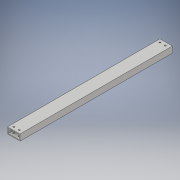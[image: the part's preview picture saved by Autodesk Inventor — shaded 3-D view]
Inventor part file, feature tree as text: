
AUTODESK INVENTOR PART (.ipt)
format: ipt  version: 2017 (Build 210142000, 142)  size: 122,880 bytes
history: native  units: in
note: dims shown in document units (in); Inventor stores cm internally (conversion verified against a paired STEP export)
features: sketch x2, extrude x1, hole x1
ambient origin geometry x8: Origin, YZ Plane, XZ Plane, XY Plane, X Axis, Y Axis, Z Axis, Center Point
bodies: Solid1 (feature_tree)
feature tree (4):
  extrude  "Extrusion1"  Depth=1.0in
  hole  "Hole1"  [1 undecoded]
  sketch  "Sketch1"  dims[d0=2.0in d1=1.0in]
  sketch  "Sketch2"  dims[d2=1.75in d3=0.75in d4=0.125in d5=0.125in d6=24.5in d7=0.0in d8=0.25in d9=90.0deg d10=0.5in d11=0.5in d12=12.25in d13=0.25in d14=0.75in d15=0.375in d16=0.25in d17=0.5635in d18=1.0in d19=0.8108in]
note: 1 required parameter value undecoded (feature->parameter linkage not recoverable at this tier; creation-order binding heuristic only, values carry confidence <= 0.55)
